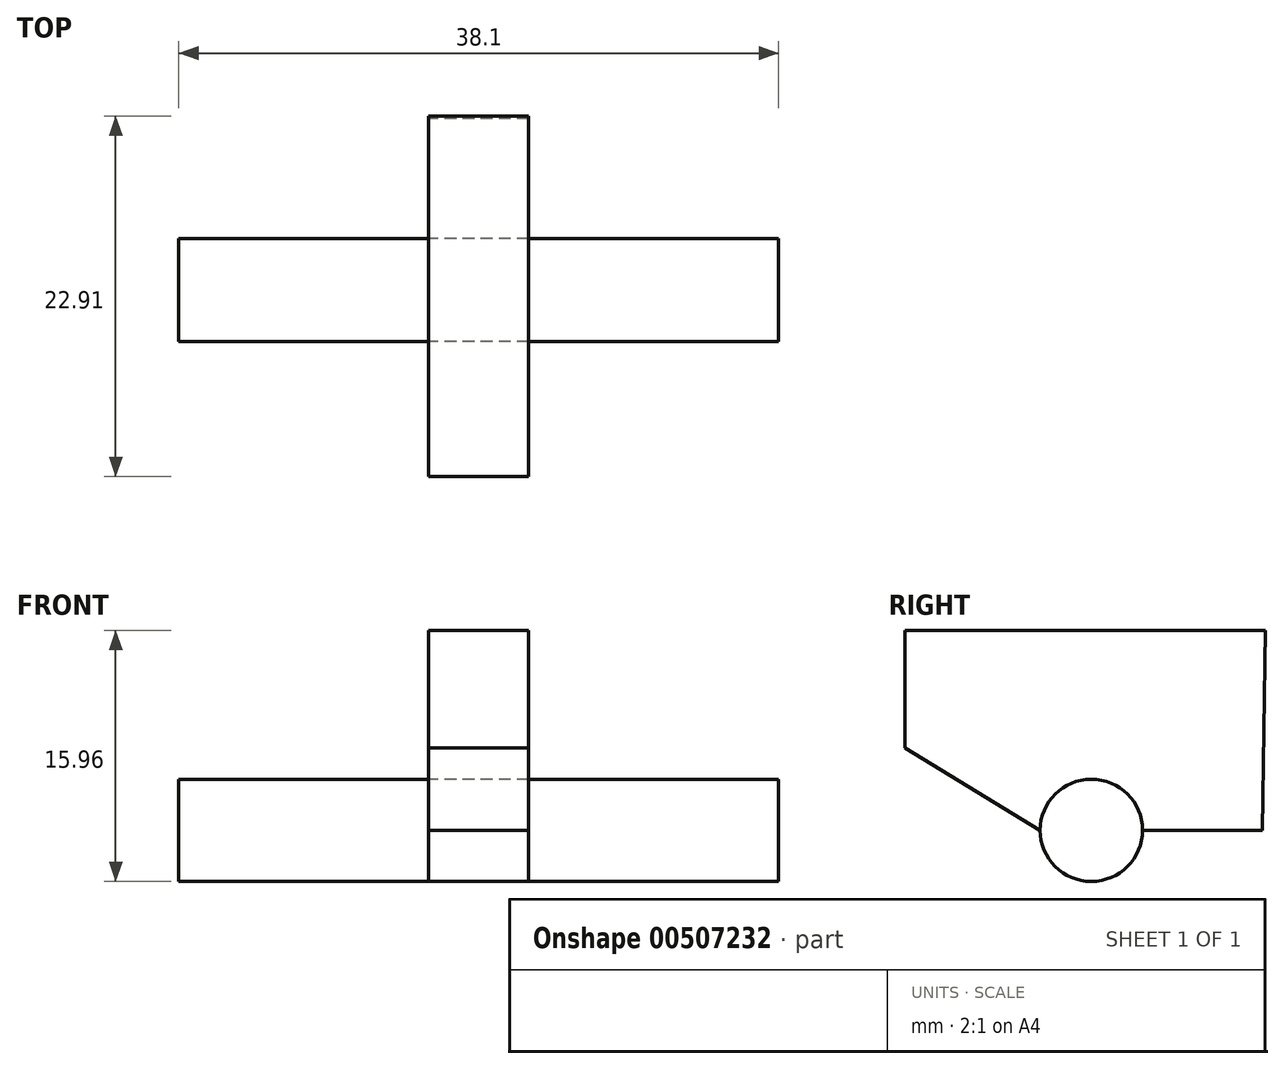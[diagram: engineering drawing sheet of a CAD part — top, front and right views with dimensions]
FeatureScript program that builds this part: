
annotation { "Feature Type Name" : "Feature", "Feature Type Description" : "" }
export const myFeature = defineFeature(function(context is Context, id is Id, definition is map)
    precondition{}
    {
        {
            var Q0;
            Q0=qCreatedBy(makeId("Right.planeOp"),FACE);
            var sketch = newSketch(context, id + "F0", { "sketchPlane" : qUnion([Q0])});
            skCircle(sketch, "E0", {"center": v(-46.67, 40.33) * mm, "radius": 3.26 * mm});
            skArc(sketch, "E1", {"start": v(-43.42, 40.33) * mm, "mid": v(-46.67, 43.57) * mm, "end": v(-49.93, 40.33) * mm});
            skLineSegment(sketch, "E2", {"start": v(-58.53, 45.55) * mm, "end": v(-58.53, 53.03) * mm});
            skLineSegment(sketch, "E3", {"start": v(-58.53, 53.03) * mm, "end": v(-35.62, 53.03) * mm});
            skLineSegment(sketch, "E4", {"start": v(-43.42, 40.33) * mm, "end": v(-35.8, 40.33) * mm});
            skLineSegment(sketch, "E5", {"start": v(-35.8, 40.33) * mm, "end": v(-35.62, 53.03) * mm});
            skLineSegment(sketch, "E6", {"start": v(-58.53, 45.55) * mm, "end": v(-49.93, 40.33) * mm});
            skSolve(sketch);
        }
        {
            var Q0;
            {var subQ0=sQuery(id+"F0.wireOp",EDGE,"E1");Q0=makeQuery(id+"F0.imprint","IMPRINT",FACE,{"disambiguationData":[TD([[makeQuery(id+"F0.imprint","IMPRINT",EDGE,{"derivedFrom":subQ0}),1.0]])]});}
            extrude(context, id + "F1", {"entities" : qUnion([Q0]), "endBound" : BoundingType.SYMMETRIC, "depth" : 38.1 * mm});
        }
        {
            var Q0;
            Q0=qSketchRegion(id+"F0",true);
            extrude(context, id + "F2", {"entities" : qUnion([Q0]), "endBound" : BoundingType.SYMMETRIC, "depth" : 6.35 * mm});
        }
    });
